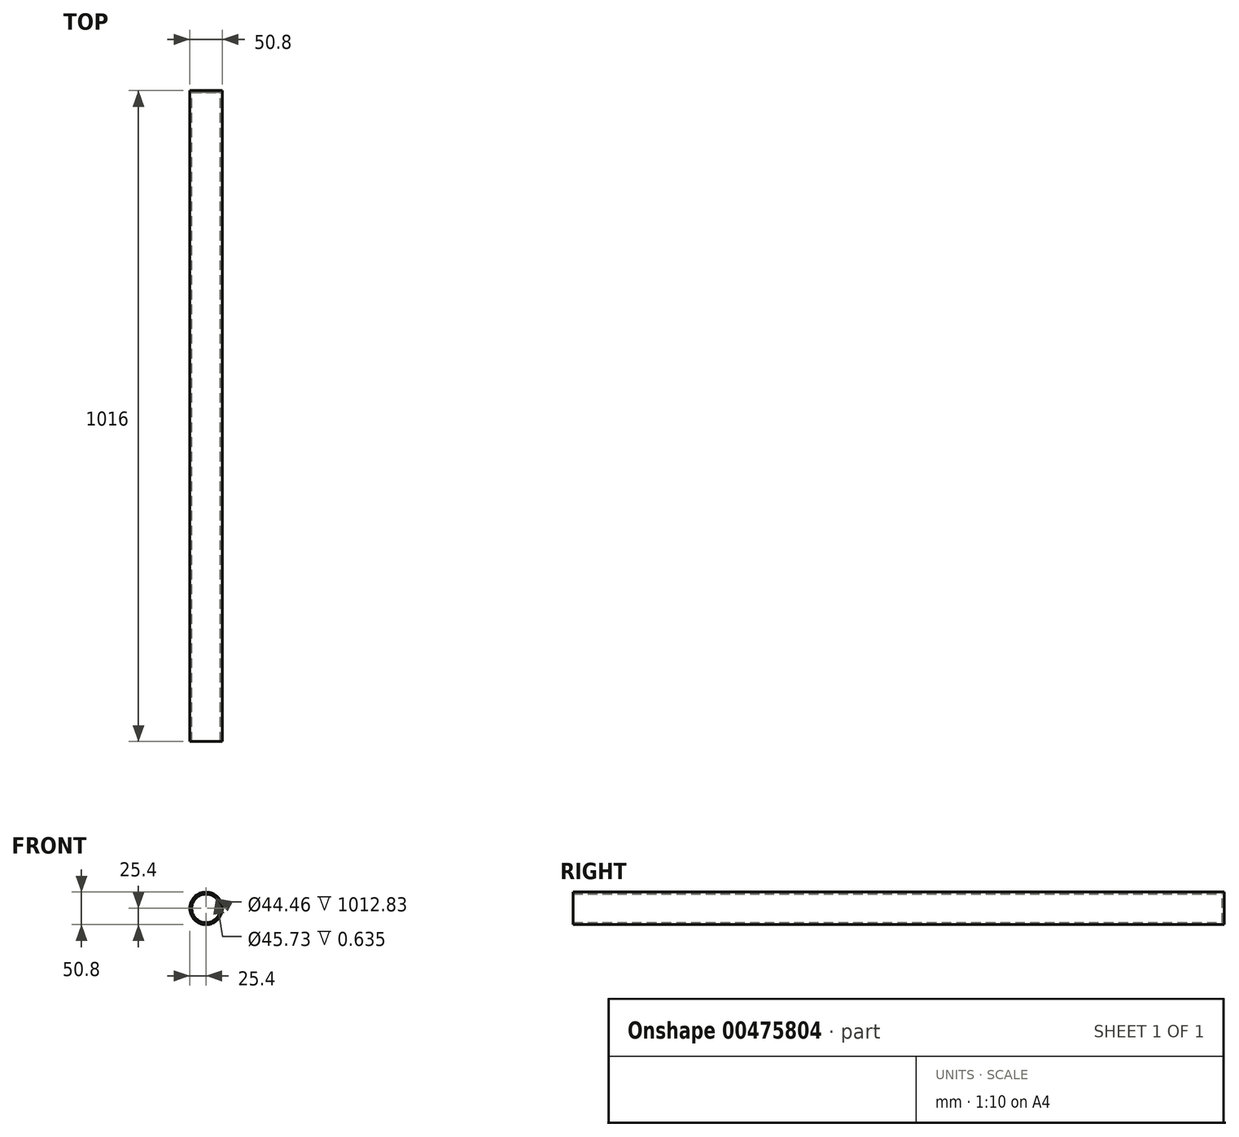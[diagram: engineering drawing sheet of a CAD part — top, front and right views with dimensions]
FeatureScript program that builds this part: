
annotation { "Feature Type Name" : "Feature", "Feature Type Description" : "" }
export const myFeature = defineFeature(function(context is Context, id is Id, definition is map)
    precondition{}
    {
        {
            var Q0;
            Q0=qCreatedBy(makeId("Front.planeOp"),FACE);
            var sketch = newSketch(context, id + "F0", { "sketchPlane" : qUnion([Q0])});
            skCircle(sketch, "E0", {"center": v(0, 0) * mm, "radius": 25.4 * mm});
            skSolve(sketch);
        }
        {
            var Q0;
            Q0=makeQuery(id+"F0.imprint","IMPRINT",FACE,{"disambiguationData":[TD([[makeQuery(id+"F0.imprint","IMPRINT",EDGE,{"derivedFrom":sQuery(id+"F0.wireOp",EDGE,"E0")}),1.0]])]});
            extrude(context, id + "F1", {"entities" : qUnion([Q0]), "depth" : 1016 * mm});
        }
        {
            var Q0;
            Q0=makeQuery(id+"F1.opExtrude","CAP_FACE",FACE,{"disambiguationData":[OSD([sQuery(id+"F0.wireOp",EDGE,"E0")])],"isStart":false});
            shell(context, id + "F2", {"entities" : qUnion([Q0]), "thickness" : 3.17 * mm});
        }
        {
            var Q0;
            Q0=makeQuery(id+"F1.opExtrude","CAP_FACE",FACE,{"disambiguationData":[OSD([sQuery(id+"F0.wireOp",EDGE,"E0")])],"isStart":true});
            shell(context, id + "F3", {"entities" : qUnion([Q0]), "thickness" : 2.54 * mm});
        }
    });
